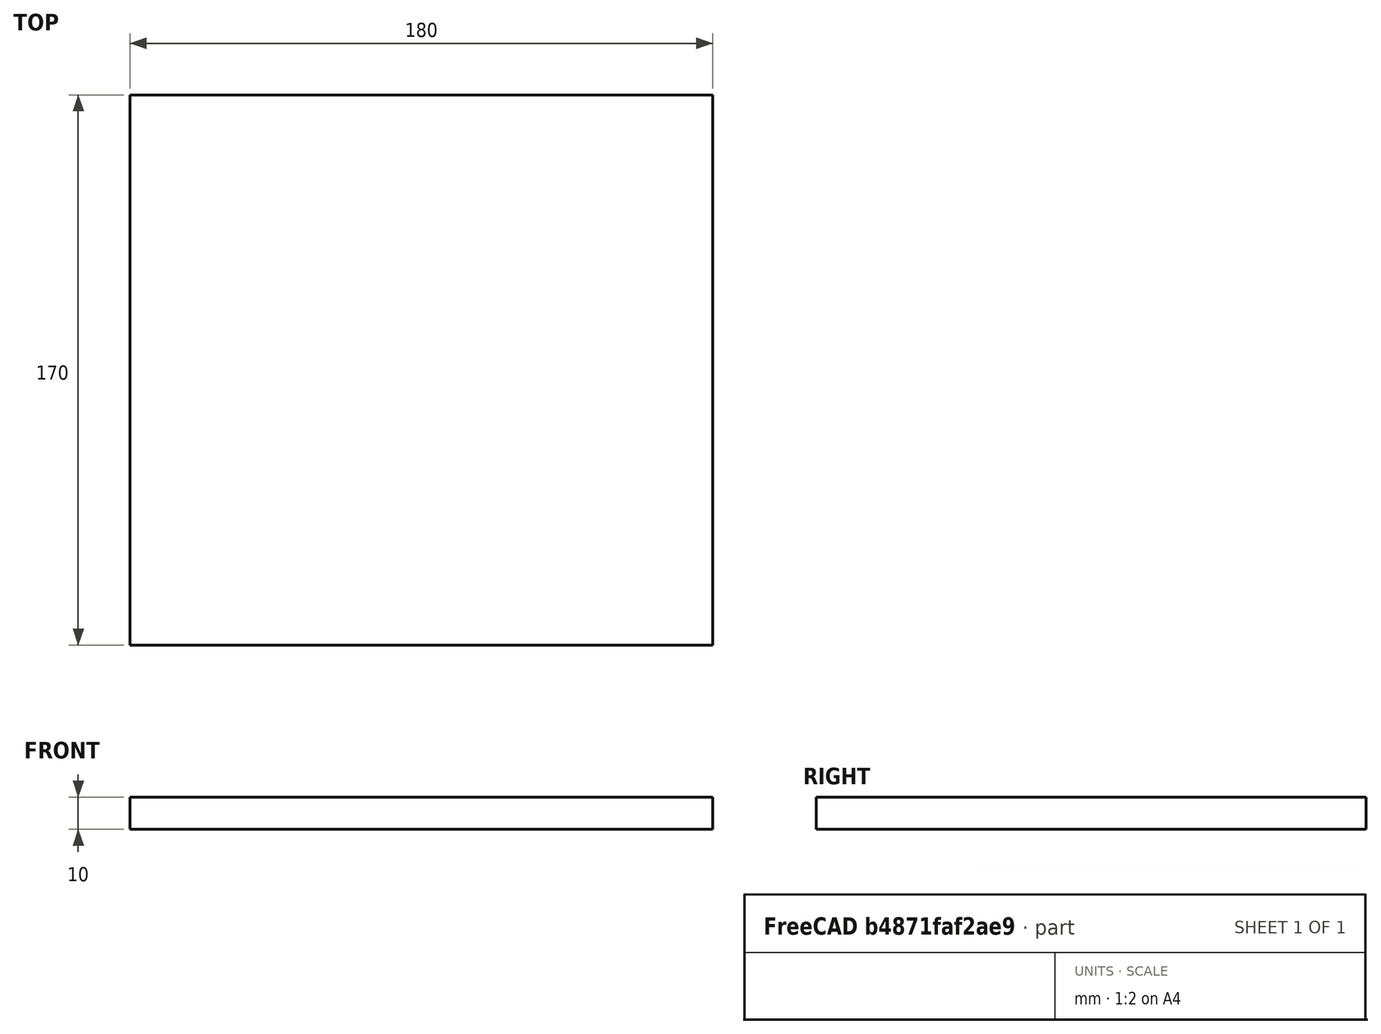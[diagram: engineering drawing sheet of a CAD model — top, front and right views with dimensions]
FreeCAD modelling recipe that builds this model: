
FCSTD DOCUMENT  (FreeCAD 0.18R4 (GitTag))
Label: TopBaseMedium
License: All rights reserved
LicenseURL: http://en.wikipedia.org/wiki/All_rights_reserved
objects: Sketcher::SketchObject×1, PartDesign::Pad×1, PartDesign::Body×1
note: 4 computed .brp shape members not serialized (recipe doc carries the construction recipe); baked Part::Feature solids carry a one-line shape summary decoded from their .brp

FEATURE [Sketcher::SketchObject] Sketch
  MapMode = 5
  Support = -> [XY_Plane]
  sketch-geometry (4):
    g0: LineSegment StartX=0 StartY=0 StartZ=0 EndX=-180 EndY=0 EndZ=0
    g1: LineSegment StartX=-180 StartY=0 StartZ=0 EndX=-180 EndY=170 EndZ=0
    g2: LineSegment StartX=-180 StartY=170 StartZ=0 EndX=0 EndY=170 EndZ=0
    g3: LineSegment StartX=0 StartY=170 StartZ=0 EndX=0 EndY=0 EndZ=0
  constraints (11):
    c: Coincident(g0,g1)
    c: Coincident(g1,g2)
    c: Coincident(g2,g3)
    c: Coincident(g3,g0)
    c: Horizontal(g0)
    c: Horizontal(g2)
    c: Vertical(g1)
    c: Vertical(g3)
    c: Distance(g3) = 170
    c: Distance(g2) = 180
    c: Coincident(g0,g-1)
FEATURE [PartDesign::Pad] Pad
  Length = 10
  Length2 = 100
  Profile = -> Sketch
  Type = 0
FEATURE [PartDesign::Body] Body
  Group = -> [Sketch,Pad]
  Origin = -> Origin
  Tip = -> Pad
